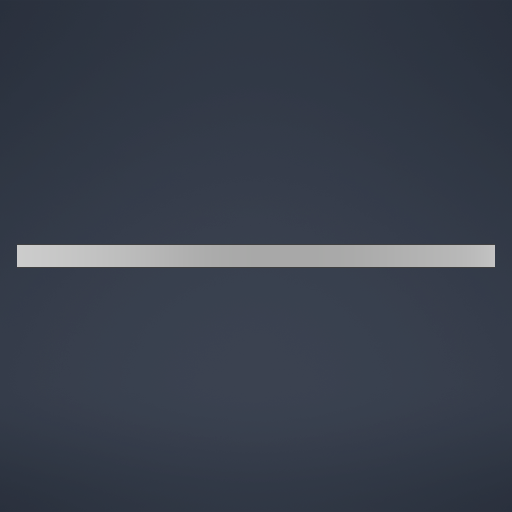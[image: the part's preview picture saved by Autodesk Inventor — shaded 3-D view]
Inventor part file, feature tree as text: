
AUTODESK INVENTOR PART (.ipt)
format: ipt  version: 2025 (Build 290162000, 162)  size: 473,600 bytes
history: native  units: in
note: dims shown in document units (in); Inventor stores cm internally (conversion verified against a paired STEP export)
features: sketch x7, extrude x5, hole x1, revolve x1
ambient origin geometry x8: Origin, YZ Plane, XZ Plane, XY Plane, X Axis, Y Axis, Z Axis, Center Point
bodies: Solid1 (feature_tree)
feature tree (14):
  sketch  "Sketch1"  dims[d0=11.811in d1=7.874in]
  extrude  "Extrusion1"  Depth=7.874in
  extrude  "Extrusion3"  Depth=0.0787in
  extrude  "Extrusion4"  Depth=3.937in TaperAngle=360.0deg
  sketch  "Sketch3"  dims[d14=0.2343in d15=3.937in d17=360.0deg]
  extrude  "Extrusion5"  Depth=11.0236in
  hole  "Hole1"  [1 undecoded]
  revolve  "Revolution1"  [1 undecoded]
  extrude  "Extrusion6"  Depth=0.0837in TaperAngle=0.0deg
  sketch  "Sketch Circular Pattern2"  dims[d8=0.0787in d9=0.0in d13=9.8425in]
  sketch  "Sketch Circular Pattern3"  dims[d19=9.498in d20=11.0236in]
  sketch  "Sketch4"  dims[d21=0.2343in d23=3.937in d25=360.0deg]
  sketch  "Sketch5"  dims[d27=0.1673in d28=0.0in d33=0.4232in d34=0.0in]
  sketch  "Sketch Circular Pattern5"  dims[d35=9.498in d36=0.0837in d37=0.0in d38=0.2343in d39=0.2362in d40=0.4124in d41=0.2904in d42=90.0deg d43=0.315in d44=0.8108in d45=0.1575in d46=0.1575in d48=0.5709in d49=0.1575in d50=0.1575in d51=360.0deg d52=0.3445in d53=0.2224in d54=0.0in d55=7.874in d56=3.937in d58=360.0deg d60=0.2343in]
note: 2 required parameter values undecoded (feature->parameter linkage not recoverable at this tier; creation-order binding heuristic only, values carry confidence <= 0.55)